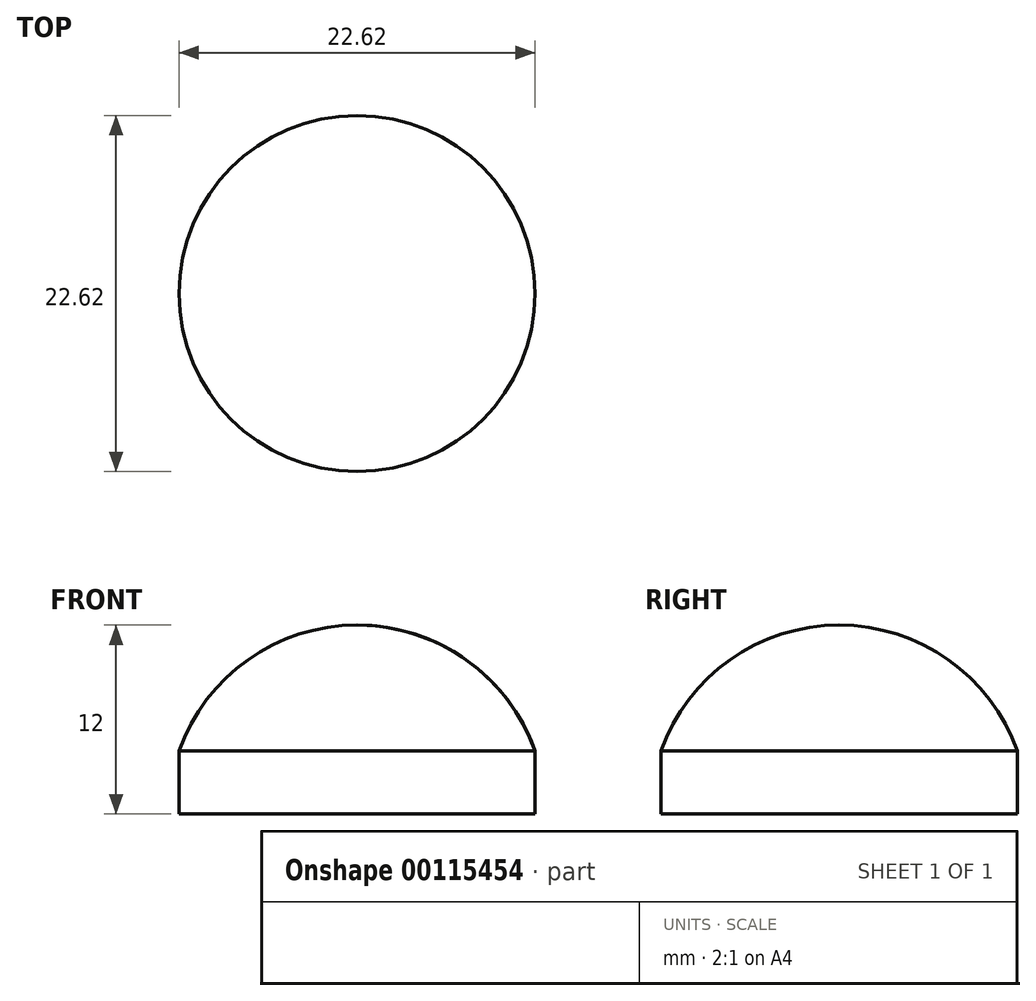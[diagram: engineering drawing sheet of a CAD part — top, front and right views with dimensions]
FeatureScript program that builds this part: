
annotation { "Feature Type Name" : "Feature", "Feature Type Description" : "" }
export const myFeature = defineFeature(function(context is Context, id is Id, definition is map)
    precondition{}
    {
        {
            var Q0;
            Q0=qCreatedBy(makeId("Front.planeOp"),FACE);
            var sketch = newSketch(context, id + "F0", { "sketchPlane" : qUnion([Q0])});
            skArc(sketch, "E0", {"start": v(0, 12) * mm, "mid": v(-6.93, 9.8) * mm, "end": v(-11.31, 4) * mm});
            skLineSegment(sketch, "E1", {"start": v(0, 4) * mm, "end": v(0, 12) * mm});
            skLineSegment(sketch, "E2", {"start": v(-11.31, 4) * mm, "end": v(-11.31, 0) * mm});
            skLineSegment(sketch, "E3", {"start": v(-11.31, 0) * mm, "end": v(0, 0) * mm});
            skLineSegment(sketch, "E4", {"start": v(0, 0) * mm, "end": v(0, 4) * mm});
            skLineSegment(sketch, "E5", {"start": v(-11.31, 4) * mm, "end": v(0, 4) * mm, "construction": true});
            skSolve(sketch);
        }
        {
            var Q0;
            Q0=makeQuery(id+"F0.imprint","IMPRINT",FACE,{"disambiguationData":[TD([[makeQuery(id+"F0.imprint","IMPRINT",EDGE,{"derivedFrom":sQuery(id+"F0.wireOp",EDGE,"E0")}),1.0]])]});
            var Q1;
            Q1=sQuery(id+"F0.wireOp",EDGE,"E1");
            revolve(context, id + "F1", {"entities" : qUnion([Q0]), "axis" : qUnion([Q1]), "revolveType" : RevolveType.FULL});
        }
    });
